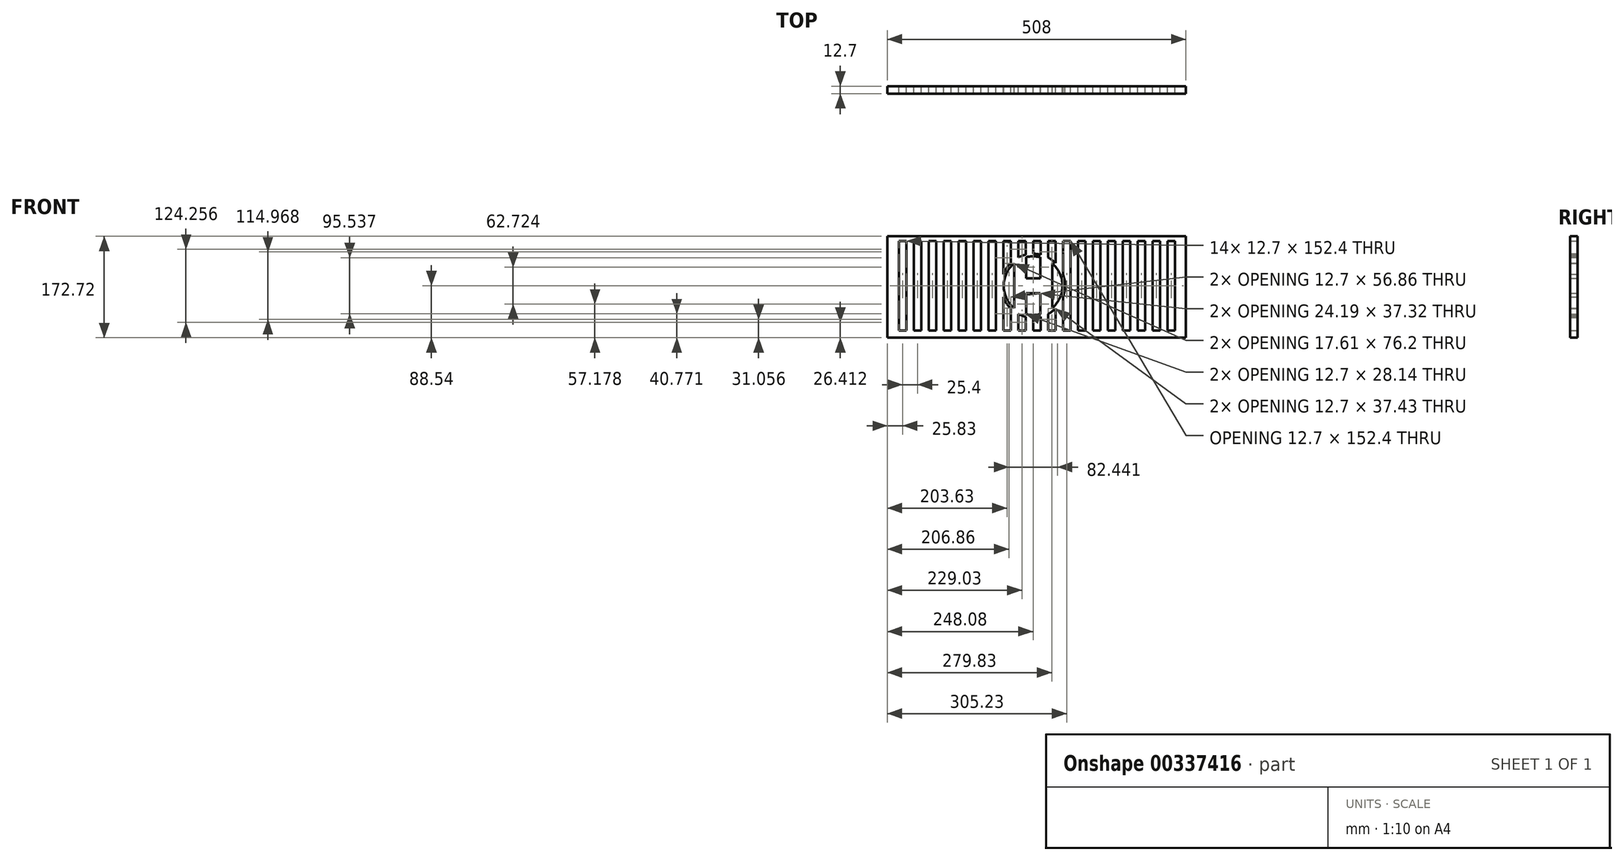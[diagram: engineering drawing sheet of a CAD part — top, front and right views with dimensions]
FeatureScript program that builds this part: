
annotation { "Feature Type Name" : "Feature", "Feature Type Description" : "" }
export const myFeature = defineFeature(function(context is Context, id is Id, definition is map)
    precondition{}
    {
        {
            var Q0;
            Q0=qCreatedBy(makeId("Front.planeOp"),FACE);
            var sketch = newSketch(context, id + "F0", { "sketchPlane" : qUnion([Q0])});
            skLineSegment(sketch, "E0.bottom", {"start": v(228.6, 76.2) * mm, "end": v(-228.6, 76.2) * mm});
            skLineSegment(sketch, "E0.top", {"start": v(228.6, -76.2) * mm, "end": v(-228.6, -76.2) * mm});
            skLineSegment(sketch, "E0.left", {"start": v(228.6, 76.2) * mm, "end": v(228.6, -76.2) * mm});
            skLineSegment(sketch, "E0.right", {"start": v(-228.6, 76.2) * mm, "end": v(-228.6, -76.2) * mm});
            skPoint(sketch, "E0.middle", {"position": v(0, 0) * mm});
            skCircle(sketch, "E1", {"center": v(0, 0) * mm, "radius": 50.02 * mm});
            skLineSegment(sketch, "E2", {"start": v(-215.9, 76.2) * mm, "end": v(-215.9, -76.2) * mm});
            skLineSegment(sketch, "E3", {"start": v(-203.2, 76.2) * mm, "end": v(-203.2, -76.2) * mm});
            skLineSegment(sketch, "E4", {"start": v(-190.5, 76.2) * mm, "end": v(-190.5, -76.2) * mm});
            skLineSegment(sketch, "E5", {"start": v(-177.8, 76.2) * mm, "end": v(-177.8, -76.2) * mm});
            skLineSegment(sketch, "E6", {"start": v(-165.1, 76.2) * mm, "end": v(-165.1, -76.2) * mm});
            skLineSegment(sketch, "E7", {"start": v(-152.4, 76.2) * mm, "end": v(-152.4, -76.2) * mm});
            skLineSegment(sketch, "E8", {"start": v(-139.7, 76.2) * mm, "end": v(-139.7, -76.2) * mm});
            skLineSegment(sketch, "E9", {"start": v(-127, 76.2) * mm, "end": v(-127, -76.2) * mm});
            skLineSegment(sketch, "E10", {"start": v(-114.3, 76.2) * mm, "end": v(-114.3, -76.2) * mm});
            skLineSegment(sketch, "E11", {"start": v(-101.6, 76.2) * mm, "end": v(-101.6, -76.2) * mm});
            skLineSegment(sketch, "E12", {"start": v(-88.9, 76.2) * mm, "end": v(-88.9, -76.2) * mm});
            skLineSegment(sketch, "E13", {"start": v(-76.2, 76.2) * mm, "end": v(-76.2, -76.2) * mm});
            skLineSegment(sketch, "E14", {"start": v(-63.5, -76.2) * mm, "end": v(-63.5, 76.2) * mm});
            skLineSegment(sketch, "E15", {"start": v(63.5, 76.2) * mm, "end": v(63.5, -76.2) * mm});
            skLineSegment(sketch, "E16", {"start": v(76.2, 76.2) * mm, "end": v(76.2, -76.2) * mm});
            skLineSegment(sketch, "E17", {"start": v(88.9, 76.2) * mm, "end": v(88.9, -76.2) * mm});
            skLineSegment(sketch, "E18", {"start": v(101.6, 76.2) * mm, "end": v(101.6, -76.2) * mm});
            skLineSegment(sketch, "E19", {"start": v(114.3, 76.2) * mm, "end": v(114.3, -76.2) * mm});
            skLineSegment(sketch, "E20", {"start": v(127, 76.2) * mm, "end": v(127, -76.2) * mm});
            skLineSegment(sketch, "E21", {"start": v(139.7, 76.2) * mm, "end": v(139.7, -76.2) * mm});
            skLineSegment(sketch, "E22", {"start": v(152.4, 76.2) * mm, "end": v(152.4, -76.2) * mm});
            skLineSegment(sketch, "E23", {"start": v(165.1, 76.2) * mm, "end": v(165.1, -76.2) * mm});
            skLineSegment(sketch, "E24", {"start": v(177.8, 76.2) * mm, "end": v(177.8, -76.2) * mm});
            skLineSegment(sketch, "E25", {"start": v(190.5, -76.2) * mm, "end": v(190.5, 76.2) * mm});
            skLineSegment(sketch, "E26", {"start": v(203.2, -76.2) * mm, "end": v(203.2, 76.2) * mm});
            skLineSegment(sketch, "E27", {"start": v(215.9, -76.2) * mm, "end": v(215.9, 76.2) * mm});
            skLineSegment(sketch, "E28", {"start": v(-32.42, 38.1) * mm, "end": v(-32.42, -38.1) * mm});
            skLineSegment(sketch, "E29", {"start": v(-32.42, -38.1) * mm, "end": v(-12.1, -38.1) * mm});
            skLineSegment(sketch, "E30", {"start": v(-12.1, -38.1) * mm, "end": v(-12.1, -12.7) * mm});
            skLineSegment(sketch, "E31", {"start": v(-12.1, -12.7) * mm, "end": v(12.1, -12.7) * mm});
            skLineSegment(sketch, "E32", {"start": v(12.1, -12.7) * mm, "end": v(12.1, -38.1) * mm});
            skLineSegment(sketch, "E33", {"start": v(12.1, -38.1) * mm, "end": v(32.42, -38.1) * mm});
            skLineSegment(sketch, "E34", {"start": v(32.42, -38.1) * mm, "end": v(32.42, 38.1) * mm});
            skLineSegment(sketch, "E35", {"start": v(32.42, 38.1) * mm, "end": v(12.1, 38.1) * mm});
            skLineSegment(sketch, "E36", {"start": v(12.1, 38.1) * mm, "end": v(12.1, 12.7) * mm});
            skLineSegment(sketch, "E37", {"start": v(12.1, 12.7) * mm, "end": v(-12.1, 12.7) * mm});
            skLineSegment(sketch, "E38", {"start": v(-12.1, 12.7) * mm, "end": v(-12.1, 38.1) * mm});
            skLineSegment(sketch, "E39", {"start": v(-12.1, 38.1) * mm, "end": v(-32.42, 38.1) * mm});
            skCircle(sketch, "E40", {"center": v(0, 0) * mm, "radius": 54.36 * mm});
            skLineSegment(sketch, "E41", {"start": v(-25.4, 76.2) * mm, "end": v(-25.4, 48.06) * mm});
            skLineSegment(sketch, "E42", {"start": v(-50.8, 76.2) * mm, "end": v(-50.8, 19.34) * mm});
            skLineSegment(sketch, "E43", {"start": v(-50.8, -76.2) * mm, "end": v(-50.8, -19.34) * mm});
            skLineSegment(sketch, "E44", {"start": v(-38.1, -76.2) * mm, "end": v(-38.1, -38.77) * mm});
            skLineSegment(sketch, "E45", {"start": v(-25.4, -76.2) * mm, "end": v(-25.4, -48.06) * mm});
            skLineSegment(sketch, "E46", {"start": v(-12.7, -76.2) * mm, "end": v(-12.7, -52.85) * mm});
            skLineSegment(sketch, "E47", {"start": v(0, -76.2) * mm, "end": v(0, -54.36) * mm});
            skLineSegment(sketch, "E48", {"start": v(12.7, -76.2) * mm, "end": v(12.7, -52.85) * mm});
            skLineSegment(sketch, "E49", {"start": v(25.4, -76.2) * mm, "end": v(25.4, -48.06) * mm});
            skLineSegment(sketch, "E50", {"start": v(38.1, -76.2) * mm, "end": v(38.1, -38.77) * mm});
            skLineSegment(sketch, "E51", {"start": v(50.8, -76.2) * mm, "end": v(50.8, -19.34) * mm});
            skLineSegment(sketch, "E52", {"start": v(50.8, 76.2) * mm, "end": v(50.8, 19.34) * mm});
            skLineSegment(sketch, "E53", {"start": v(38.1, 76.2) * mm, "end": v(38.1, 38.77) * mm});
            skLineSegment(sketch, "E54", {"start": v(25.4, 76.2) * mm, "end": v(25.4, 48.06) * mm});
            skLineSegment(sketch, "E55", {"start": v(12.7, 76.2) * mm, "end": v(12.7, 52.85) * mm});
            skLineSegment(sketch, "E56", {"start": v(0, 76.2) * mm, "end": v(0, 54.36) * mm});
            skLineSegment(sketch, "E57", {"start": v(-12.7, 76.2) * mm, "end": v(-12.7, 52.85) * mm});
            skLineSegment(sketch, "E58", {"start": v(-38.1, 76.2) * mm, "end": v(-38.1, 38.77) * mm});
            skLineSegment(sketch, "E59", {"start": v(228.6, 76.2) * mm, "end": v(241.3, 76.2) * mm});
            skLineSegment(sketch, "E60", {"start": v(228.6, -76.2) * mm, "end": v(241.3, -76.2) * mm});
            skLineSegment(sketch, "E61", {"start": v(241.3, 76.2) * mm, "end": v(241.3, -76.2) * mm});
            skLineSegment(sketch, "E62", {"start": v(-248.08, 84.18) * mm, "end": v(-248.08, -88.54) * mm});
            skLineSegment(sketch, "E63", {"start": v(-248.08, -88.54) * mm, "end": v(259.92, -88.54) * mm});
            skLineSegment(sketch, "E64", {"start": v(259.92, -88.54) * mm, "end": v(259.92, 84.18) * mm});
            skLineSegment(sketch, "E65", {"start": v(-248.08, 84.18) * mm, "end": v(259.92, 84.18) * mm});
            skLineSegment(sketch, "E66", {"start": v(-12.1, 38.1) * mm, "end": v(-12.1, 48.54) * mm});
            skLineSegment(sketch, "E67", {"start": v(12.1, 38.1) * mm, "end": v(12.1, 48.54) * mm});
            skLineSegment(sketch, "E68", {"start": v(-12.1, -38.1) * mm, "end": v(-12.1, -48.54) * mm});
            skLineSegment(sketch, "E69", {"start": v(12.1, -38.1) * mm, "end": v(12.1, -48.54) * mm});
            skSolve(sketch);
        }
        {
            var Q0;
            {var subQ0=sQuery(id+"F0.wireOp",EDGE,"E2");Q0=makeQuery(id+"F0.imprint","IMPRINT",FACE,{"disambiguationData":[TD([[makeQuery(id+"F0.imprint","IMPRINT",EDGE,{"derivedFrom":subQ0}),1.0]])]});}
            var Q1;
            {var subQ0=sQuery(id+"F0.wireOp",EDGE,"E4");Q1=makeQuery(id+"F0.imprint","IMPRINT",FACE,{"disambiguationData":[TD([[makeQuery(id+"F0.imprint","IMPRINT",EDGE,{"derivedFrom":subQ0}),1.0]])]});}
            var Q2;
            {var subQ0=sQuery(id+"F0.wireOp",EDGE,"E6");Q2=makeQuery(id+"F0.imprint","IMPRINT",FACE,{"disambiguationData":[TD([[makeQuery(id+"F0.imprint","IMPRINT",EDGE,{"derivedFrom":subQ0}),1.0]])]});}
            var Q3;
            {var subQ0=sQuery(id+"F0.wireOp",EDGE,"E8");Q3=makeQuery(id+"F0.imprint","IMPRINT",FACE,{"disambiguationData":[TD([[makeQuery(id+"F0.imprint","IMPRINT",EDGE,{"derivedFrom":subQ0}),1.0]])]});}
            var Q4;
            {var subQ0=sQuery(id+"F0.wireOp",EDGE,"E10");Q4=makeQuery(id+"F0.imprint","IMPRINT",FACE,{"disambiguationData":[TD([[makeQuery(id+"F0.imprint","IMPRINT",EDGE,{"derivedFrom":subQ0}),1.0]])]});}
            var Q5;
            {var subQ0=sQuery(id+"F0.wireOp",EDGE,"E12");Q5=makeQuery(id+"F0.imprint","IMPRINT",FACE,{"disambiguationData":[TD([[makeQuery(id+"F0.imprint","IMPRINT",EDGE,{"derivedFrom":subQ0}),1.0]])]});}
            var Q6;
            {var subQ0=sQuery(id+"F0.wireOp",EDGE,"E14");Q6=makeQuery(id+"F0.imprint","IMPRINT",FACE,{"disambiguationData":[TD([[makeQuery(id+"F0.imprint","IMPRINT",EDGE,{"derivedFrom":subQ0}),-1.0]])]});}
            var Q7;
            {var subQ0=sQuery(id+"F0.wireOp",EDGE,"Inqf0u7s-2Z19-imyh-WJYn-TEZLkkLsL724");Q7=makeQuery(id+"F0.imprint","IMPRINT",FACE,{"disambiguationData":[TD([[makeQuery(id+"F0.imprint","IMPRINT",EDGE,{"derivedFrom":subQ0}),1.0]])]});}
            var Q8;
            {var subQ0=sQuery(id+"F0.wireOp",EDGE,"d5CL29Ya-ZK6t-85xp-HYht-tH2Sqx6XHoZV");Q8=makeQuery(id+"F0.imprint","IMPRINT",FACE,{"disambiguationData":[TD([[makeQuery(id+"F0.imprint","IMPRINT",EDGE,{"derivedFrom":subQ0}),1.0]])]});}
            var Q9;
            {var subQ0=sQuery(id+"F0.wireOp",EDGE,"qIBniEWp-SjWG-6MvS-6QwP-yGmgbxBXBY1j");Q9=makeQuery(id+"F0.imprint","IMPRINT",FACE,{"disambiguationData":[TD([[makeQuery(id+"F0.imprint","IMPRINT",EDGE,{"derivedFrom":subQ0}),1.0]])]});}
            var Q10;
            {var subQ0=sQuery(id+"F0.wireOp",EDGE,"wc19tvvr-HGr4-4w4J-CDzH-Us4qWI36HlVF");Q10=makeQuery(id+"F0.imprint","IMPRINT",FACE,{"disambiguationData":[TD([[makeQuery(id+"F0.imprint","IMPRINT",EDGE,{"derivedFrom":subQ0}),1.0]])]});}
            var Q11;
            {var subQ0=sQuery(id+"F0.wireOp",EDGE,"E15");Q11=makeQuery(id+"F0.imprint","IMPRINT",FACE,{"disambiguationData":[TD([[makeQuery(id+"F0.imprint","IMPRINT",EDGE,{"derivedFrom":subQ0}),1.0]])]});}
            var Q12;
            {var subQ0=sQuery(id+"F0.wireOp",EDGE,"E17");Q12=makeQuery(id+"F0.imprint","IMPRINT",FACE,{"disambiguationData":[TD([[makeQuery(id+"F0.imprint","IMPRINT",EDGE,{"derivedFrom":subQ0}),1.0]])]});}
            var Q13;
            {var subQ0=sQuery(id+"F0.wireOp",EDGE,"E19");Q13=makeQuery(id+"F0.imprint","IMPRINT",FACE,{"disambiguationData":[TD([[makeQuery(id+"F0.imprint","IMPRINT",EDGE,{"derivedFrom":subQ0}),1.0]])]});}
            var Q14;
            {var subQ0=sQuery(id+"F0.wireOp",EDGE,"E21");Q14=makeQuery(id+"F0.imprint","IMPRINT",FACE,{"disambiguationData":[TD([[makeQuery(id+"F0.imprint","IMPRINT",EDGE,{"derivedFrom":subQ0}),1.0]])]});}
            var Q15;
            {var subQ0=sQuery(id+"F0.wireOp",EDGE,"E23");Q15=makeQuery(id+"F0.imprint","IMPRINT",FACE,{"disambiguationData":[TD([[makeQuery(id+"F0.imprint","IMPRINT",EDGE,{"derivedFrom":subQ0}),1.0]])]});}
            var Q16;
            {var subQ0=sQuery(id+"F0.wireOp",EDGE,"E25");Q16=makeQuery(id+"F0.imprint","IMPRINT",FACE,{"disambiguationData":[TD([[makeQuery(id+"F0.imprint","IMPRINT",EDGE,{"derivedFrom":subQ0}),-1.0]])]});}
            var Q17;
            {var subQ0=sQuery(id+"F0.wireOp",EDGE,"E0.left");Q17=makeQuery(id+"F0.imprint","IMPRINT",FACE,{"disambiguationData":[TD([[makeQuery(id+"F0.imprint","IMPRINT",EDGE,{"derivedFrom":subQ0}),-1.0]])]});}
            var Q18;
            {var subQ0=sQuery(id+"F0.wireOp",EDGE,"298UEcsp-zSOG-EBNW-fSEO-aJqaI1nw5KVv");Q18=makeQuery(id+"F0.imprint","IMPRINT",FACE,{"disambiguationData":[TD([[makeQuery(id+"F0.imprint","IMPRINT",EDGE,{"derivedFrom":subQ0}),1.0]])]});}
            var Q19;
            {var subQ0=sQuery(id+"F0.wireOp",EDGE,"b8S822ZE-PwCn-39aQ-T1LJ-F65aP3EX0ssb");Q19=makeQuery(id+"F0.imprint","IMPRINT",FACE,{"disambiguationData":[TD([[makeQuery(id+"F0.imprint","IMPRINT",EDGE,{"derivedFrom":subQ0}),1.0]])]});}
            var Q20;
            {var subQ0=sQuery(id+"F0.wireOp",EDGE,"H1sGl2HI-CLsP-3FbA-XK4L-uGxBEb8ZSNLr");Q20=makeQuery(id+"F0.imprint","IMPRINT",FACE,{"disambiguationData":[TD([[makeQuery(id+"F0.imprint","IMPRINT",EDGE,{"derivedFrom":subQ0}),1.0]])]});}
            var Q21;
            Q21=makeQuery(id+"F0.imprint","IMPRINT",FACE,{"disambiguationData":[TD([[makeQuery(id+"F0.imprint","IMPRINT",EDGE,{"derivedFrom":sQuery(id+"F0.wireOp",EDGE,"E28")}),1.0]])]});
            var Q22;
            {var subQ0=sQuery(id+"F0.wireOp",EDGE,"E41");Q22=makeQuery(id+"F0.imprint","IMPRINT",FACE,{"disambiguationData":[TD([[makeQuery(id+"F0.imprint","IMPRINT",EDGE,{"derivedFrom":subQ0}),-1.0]])]});}
            var Q23;
            {var subQ0=sQuery(id+"F0.wireOp",EDGE,"E56");Q23=makeQuery(id+"F0.imprint","IMPRINT",FACE,{"disambiguationData":[TD([[makeQuery(id+"F0.imprint","IMPRINT",EDGE,{"derivedFrom":subQ0}),-1.0]])]});}
            var Q24;
            {var subQ0=sQuery(id+"F0.wireOp",EDGE,"E54");Q24=makeQuery(id+"F0.imprint","IMPRINT",FACE,{"disambiguationData":[TD([[makeQuery(id+"F0.imprint","IMPRINT",EDGE,{"derivedFrom":subQ0}),-1.0]])]});}
            var Q25;
            {var subQ0=sQuery(id+"F0.wireOp",EDGE,"E52");Q25=makeQuery(id+"F0.imprint","IMPRINT",FACE,{"disambiguationData":[TD([[makeQuery(id+"F0.imprint","IMPRINT",EDGE,{"derivedFrom":subQ0}),-1.0]])]});}
            var Q26;
            {var subQ0=sQuery(id+"F0.wireOp",EDGE,"E40");var subQ6=makeQuery(id+"F0.imprint","INTERSECT",VERTEX,{"derivedFrom":[subQ0,sQuery(id+"F0.wireOp",EDGE,"E52")]});Q26=makeQuery(id+"F0.imprint","IMPRINT",FACE,{"disambiguationData":[TD([[makeQuery(id+"F0.imprint","IMPRINT",EDGE,{"disambiguationData":[TD([[subQ6,-1.0]])],"derivedFrom":subQ0}),1.0]])]});}
            var Q27;
            {var subQ0=sQuery(id+"F0.wireOp",EDGE,"E50");Q27=makeQuery(id+"F0.imprint","IMPRINT",FACE,{"disambiguationData":[TD([[makeQuery(id+"F0.imprint","IMPRINT",EDGE,{"derivedFrom":subQ0}),-1.0]])]});}
            var Q28;
            {var subQ0=sQuery(id+"F0.wireOp",EDGE,"E48");Q28=makeQuery(id+"F0.imprint","IMPRINT",FACE,{"disambiguationData":[TD([[makeQuery(id+"F0.imprint","IMPRINT",EDGE,{"derivedFrom":subQ0}),-1.0]])]});}
            var Q29;
            {var subQ0=sQuery(id+"F0.wireOp",EDGE,"E46");Q29=makeQuery(id+"F0.imprint","IMPRINT",FACE,{"disambiguationData":[TD([[makeQuery(id+"F0.imprint","IMPRINT",EDGE,{"derivedFrom":subQ0}),-1.0]])]});}
            var Q30;
            {var subQ0=sQuery(id+"F0.wireOp",EDGE,"E44");Q30=makeQuery(id+"F0.imprint","IMPRINT",FACE,{"disambiguationData":[TD([[makeQuery(id+"F0.imprint","IMPRINT",EDGE,{"derivedFrom":subQ0}),-1.0]])]});}
            var Q31;
            {var subQ23=sQuery(id+"F0.wireOp",EDGE,"E0.right");Q31=makeQuery(id+"F0.imprint","IMPRINT",FACE,{"disambiguationData":[TD([[makeQuery(id+"F0.imprint","IMPRINT",EDGE,{"derivedFrom":subQ23}),-1.0]])]});}
            var Q32;
            {var subQ0=sQuery(id+"F0.wireOp",EDGE,"E39");Q32=makeQuery(id+"F0.imprint","IMPRINT",FACE,{"disambiguationData":[TD([[makeQuery(id+"F0.imprint","IMPRINT",EDGE,{"derivedFrom":subQ0}),-1.0]])]});}
            var Q33;
            {var subQ0=sQuery(id+"F0.wireOp",EDGE,"E35");Q33=makeQuery(id+"F0.imprint","IMPRINT",FACE,{"disambiguationData":[TD([[makeQuery(id+"F0.imprint","IMPRINT",EDGE,{"derivedFrom":subQ0}),-1.0]])]});}
            var Q34;
            {var subQ0=sQuery(id+"F0.wireOp",EDGE,"E33");Q34=makeQuery(id+"F0.imprint","IMPRINT",FACE,{"disambiguationData":[TD([[makeQuery(id+"F0.imprint","IMPRINT",EDGE,{"derivedFrom":subQ0}),-1.0]])]});}
            var Q35;
            {var subQ0=sQuery(id+"F0.wireOp",EDGE,"E29");Q35=makeQuery(id+"F0.imprint","IMPRINT",FACE,{"disambiguationData":[TD([[makeQuery(id+"F0.imprint","IMPRINT",EDGE,{"derivedFrom":subQ0}),-1.0]])]});}
            extrude(context, id + "F1", {"entities" : qUnion([Q0, Q1, Q2, Q3, Q4, Q5, Q6, Q7, Q8, Q9, Q10, Q11, Q12, Q13, Q14, Q15, Q16, Q17, Q18, Q19, Q20, Q21, Q22, Q23, Q24, Q25, Q26, Q27, Q28, Q29, Q30, Q31, Q32, Q33, Q34, Q35]), "depth" : 12.7 * mm});
        }
    });
